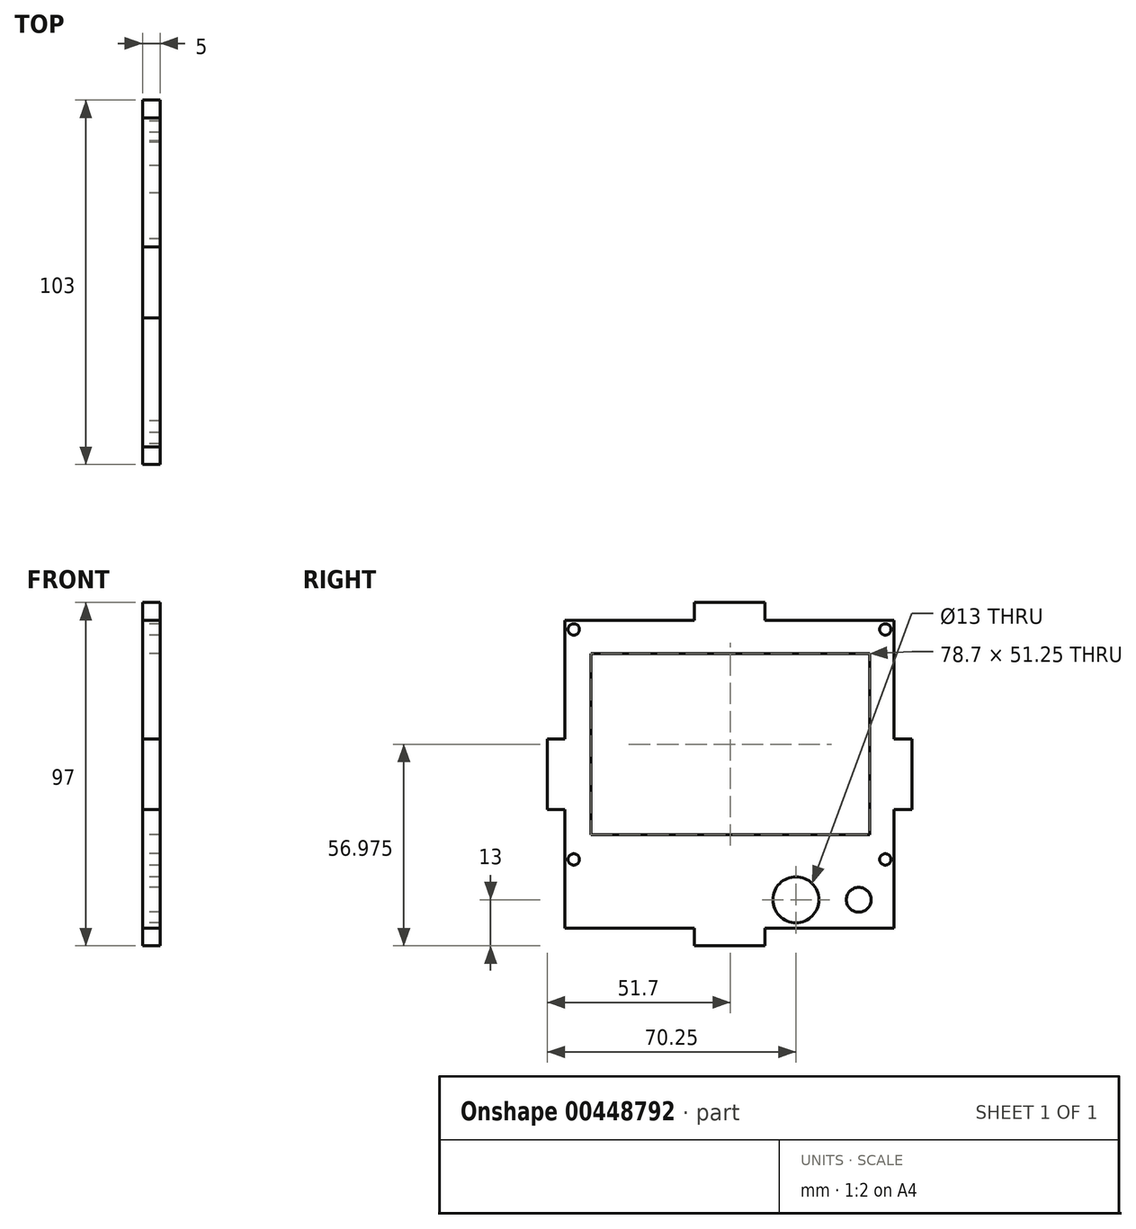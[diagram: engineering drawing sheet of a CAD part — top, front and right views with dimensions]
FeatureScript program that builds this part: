
annotation { "Feature Type Name" : "Feature", "Feature Type Description" : "" }
export const myFeature = defineFeature(function(context is Context, id is Id, definition is map)
    precondition{}
    {
        {
            assignVariable(context, id + "F0", {"name" : "thickness", "anyValue" : 5 * mm});
        }
        {
            var Q0;
            Q0=qCreatedBy(makeId("Right.planeOp"),FACE);
            var sketch = newSketch(context, id + "F1", { "sketchPlane" : qUnion([Q0])});
            skLineSegment(sketch, "E0.bottom", {"start": v(0, 87) * mm, "end": v(93, 87) * mm});
            skLineSegment(sketch, "E0.top", {"start": v(0, 0) * mm, "end": v(93, 0) * mm});
            skLineSegment(sketch, "E0.left", {"start": v(0, 87) * mm, "end": v(0, 0) * mm});
            skLineSegment(sketch, "E0.right", {"start": v(93, 87) * mm, "end": v(93, 0) * mm});
            skPoint(sketch, "E1.centerSnap0", {"position": v(0, 43.5) * mm});
            skLineSegment(sketch, "E2", {"start": v(-5, 53.5) * mm, "end": v(0, 53.5) * mm});
            skLineSegment(sketch, "E3", {"start": v(-5, 33.5) * mm, "end": v(0, 33.5) * mm});
            skLineSegment(sketch, "E4.trimOffspring", {"start": v(-5, 53.5) * mm, "end": v(-5, 33.5) * mm});
            skLineSegment(sketch, "E5", {"start": v(46.5, 92) * mm, "end": v(46.5, -5) * mm, "construction": true});
            skLineSegment(sketch, "E6", {"start": v(93, 43.5) * mm, "end": v(0, 43.5) * mm, "construction": true});
            skLineSegment(sketch, "E7.MirrorCS", {"start": v(98, 53.5) * mm, "end": v(93, 53.5) * mm});
            skLineSegment(sketch, "E8.MirrorCS", {"start": v(98, 53.5) * mm, "end": v(98, 33.5) * mm});
            skLineSegment(sketch, "E9.MirrorCS", {"start": v(98, 33.5) * mm, "end": v(93, 33.5) * mm});
            skPoint(sketch, "E10.MirrorP", {"position": v(93, 43.5) * mm});
            skLineSegment(sketch, "E11.bottom", {"start": v(7.35, 77.6) * mm, "end": v(86.05, 77.6) * mm});
            skLineSegment(sketch, "E11.top", {"start": v(7.35, 26.35) * mm, "end": v(86.05, 26.35) * mm});
            skLineSegment(sketch, "E11.left", {"start": v(7.35, 77.6) * mm, "end": v(7.35, 26.35) * mm});
            skLineSegment(sketch, "E11.right", {"start": v(86.05, 77.6) * mm, "end": v(86.05, 26.35) * mm});
            skCircle(sketch, "E12", {"center": v(83, 8) * mm, "radius": 3.5 * mm});
            skCircle(sketch, "E13", {"center": v(65.25, 8) * mm, "radius": 6.5 * mm});
            skLineSegment(sketch, "E14", {"start": v(36.5, 92) * mm, "end": v(36.5, 87) * mm});
            skLineSegment(sketch, "E15", {"start": v(56.5, 92) * mm, "end": v(56.5, 87) * mm});
            skLineSegment(sketch, "E16.trimOffspring", {"start": v(36.5, 92) * mm, "end": v(56.5, 92) * mm});
            skLineSegment(sketch, "E17.MirrorCS", {"start": v(56.5, -5) * mm, "end": v(56.5, 0) * mm});
            skLineSegment(sketch, "E18.MirrorCS", {"start": v(36.5, -5) * mm, "end": v(56.5, -5) * mm});
            skLineSegment(sketch, "E19.MirrorCS", {"start": v(36.5, -5) * mm, "end": v(36.5, 0) * mm});
            skCircle(sketch, "E20", {"center": v(2.5, 19.4) * mm, "radius": 1.6 * mm});
            skCircle(sketch, "E21", {"center": v(2.5, 84.4) * mm, "radius": 1.6 * mm});
            skCircle(sketch, "E22", {"center": v(90.5, 84.4) * mm, "radius": 1.6 * mm});
            skCircle(sketch, "E23", {"center": v(90.5, 19.4) * mm, "radius": 1.6 * mm});
            skLineSegment(sketch, "E24", {"start": v(2.5, 84.4) * mm, "end": v(90.5, 84.4) * mm, "construction": true});
            skPoint(sketch, "E25", {"position": v(46.5, 84.4) * mm});
            skSolve(sketch);
        }
        {
            var Q0;
            Q0=qSketchRegion(id+"F1",true);
            extrude(context, id + "F2", {"entities" : qUnion([Q0]), "depth" : getVariable(context, 'thickness')});
        }
    });
